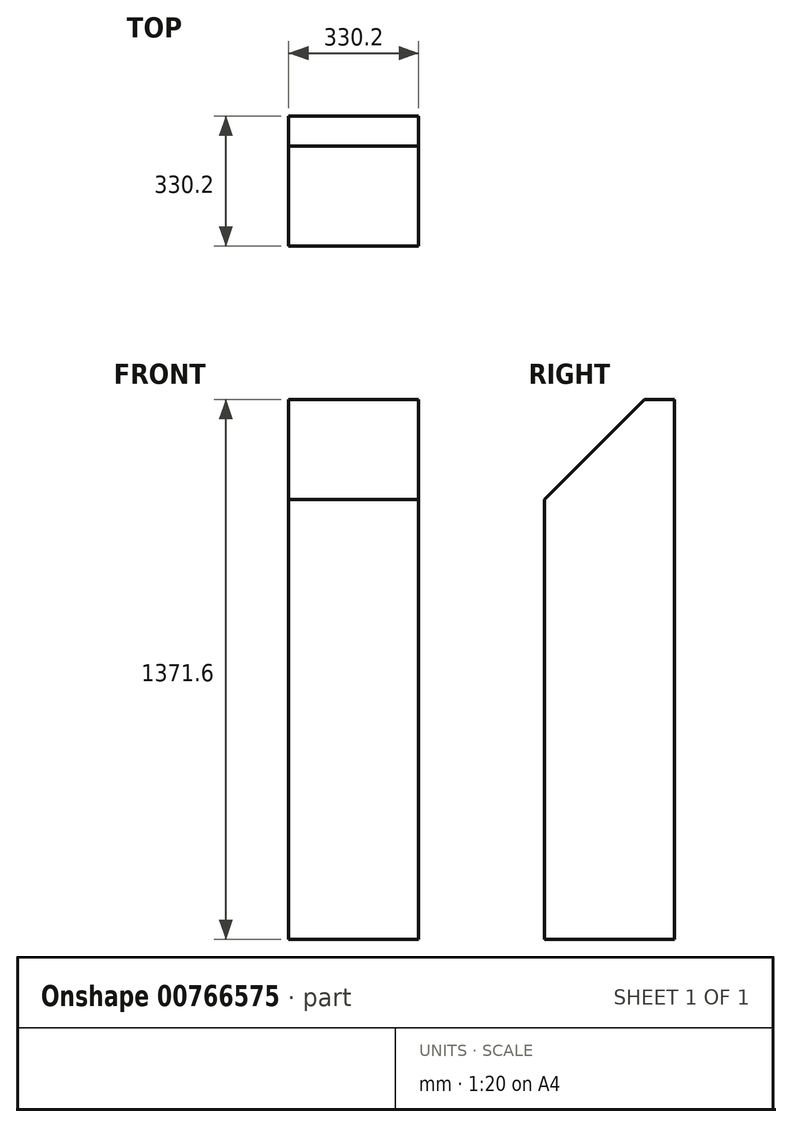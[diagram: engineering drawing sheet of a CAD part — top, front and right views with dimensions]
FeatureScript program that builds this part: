
annotation { "Feature Type Name" : "Feature", "Feature Type Description" : "" }
export const myFeature = defineFeature(function(context is Context, id is Id, definition is map)
    precondition{}
    {
        {
            var Q0;
            Q0=qCreatedBy(makeId("Top.planeOp"),FACE);
            var sketch = newSketch(context, id + "F0", { "sketchPlane" : qUnion([Q0])});
            skLineSegment(sketch, "E0.bottom", {"start": v(-165.1, 165.1) * mm, "end": v(165.1, 165.1) * mm});
            skLineSegment(sketch, "E0.top", {"start": v(-165.1, -165.1) * mm, "end": v(165.1, -165.1) * mm});
            skLineSegment(sketch, "E0.left", {"start": v(-165.1, 165.1) * mm, "end": v(-165.1, -165.1) * mm});
            skLineSegment(sketch, "E0.right", {"start": v(165.1, 165.1) * mm, "end": v(165.1, -165.1) * mm});
            skLineSegment(sketch, "E1", {"start": v(-165.1, 165.1) * mm, "end": v(165.1, -165.1) * mm, "construction": true});
            skSolve(sketch);
        }
        {
            var Q0;
            Q0 = qSketchRegion(id + "F0", true);
            extrude(context, id + "F1", {"entities" : qUnion([Q0]), "depth" : 1371.6 * mm, "offsetDistance" : 25.4 * mm});
        }
        {
            var Q0;
            Q0=makeQuery(id+"F1.opExtrude","CAP_EDGE",EDGE,{"disambiguationData":[OSD([sQuery(id+"F0.wireOp",EDGE,"E0.top")])],"isStart":false});
            chamfer(context, id + "F2", {"entities" : qUnion([Q0]), "width" : 254 * mm, "tangentPropagation" : true});
        }
    });
